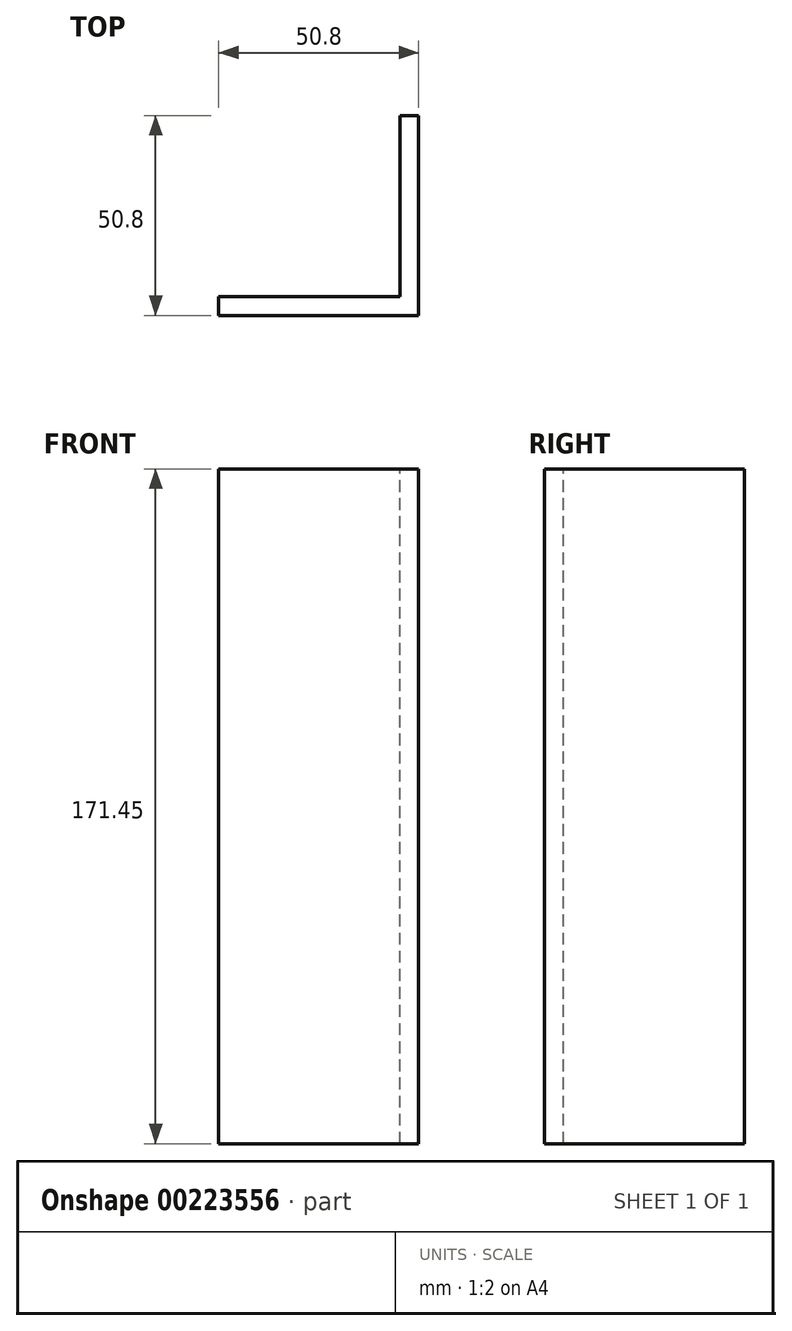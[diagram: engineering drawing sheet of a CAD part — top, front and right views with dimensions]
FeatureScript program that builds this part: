
annotation { "Feature Type Name" : "Feature", "Feature Type Description" : "" }
export const myFeature = defineFeature(function(context is Context, id is Id, definition is map)
    precondition{}
    {
        {
            var Q0;
            Q0=qCreatedBy(makeId("Top.planeOp"),FACE);
            var sketch = newSketch(context, id + "F0", { "sketchPlane" : qUnion([Q0])});
            skLineSegment(sketch, "E0.bottom", {"start": v(42.27, -27.58) * mm, "end": v(-8.53, -27.58) * mm});
            skLineSegment(sketch, "E0.top", {"start": v(42.27, 23.22) * mm, "end": v(-8.53, 23.22) * mm});
            skLineSegment(sketch, "E0.left", {"start": v(42.27, -27.58) * mm, "end": v(42.27, 23.22) * mm});
            skLineSegment(sketch, "E0.right", {"start": v(-8.53, -27.58) * mm, "end": v(-8.53, 23.22) * mm});
            skSolve(sketch);
        }
        {
            var Q0;
            Q0 = qSketchRegion(id + "F0", true);
            extrude(context, id + "F1", {"entities" : qUnion([Q0]), "oppositeDirection" : true, "depth" : 171.45 * mm});
        }
        {
            var Q0;
            Q0=makeQuery(id+"F1.opExtrude","CAP_FACE",FACE,{"disambiguationData":[OSD([sQuery(id+"F0.wireOp",EDGE,"E0.bottom"),sQuery(id+"F0.wireOp",EDGE,"E0.top"),sQuery(id+"F0.wireOp",EDGE,"E0.left"),sQuery(id+"F0.wireOp",EDGE,"E0.right")])],"isStart":true});
            var sketch = newSketch(context, id + "F2", { "sketchPlane" : qUnion([Q0])});
            skLineSegment(sketch, "E1.bottom", {"start": v(-8.53, 23.22) * mm, "end": v(37.5, 23.22) * mm});
            skLineSegment(sketch, "E1.top", {"start": v(-8.53, -22.82) * mm, "end": v(37.5, -22.82) * mm});
            skLineSegment(sketch, "E1.left", {"start": v(-8.53, 23.22) * mm, "end": v(-8.53, -22.82) * mm});
            skLineSegment(sketch, "E1.right", {"start": v(37.5, 23.22) * mm, "end": v(37.5, -22.82) * mm});
            skSolve(sketch);
        }
        {
            var Q0;
            Q0 = qSketchRegion(id + "F2", true);
            extrude(context, id + "F3", {"entities" : qUnion([Q0]), "operationType" : NewBodyOperationType.REMOVE, "endBound" : BoundingType.THROUGH_ALL, "oppositeDirection" : true, "depth" : 25.4 * mm});
        }
    });
